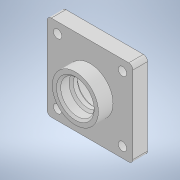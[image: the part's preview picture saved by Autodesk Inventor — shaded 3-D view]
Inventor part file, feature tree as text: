
AUTODESK INVENTOR PART (.ipt)
format: ipt  version: 2022 (Build 260153000, 153)  size: 163,840 bytes
history: native  units: mm
features: sketch x4, extrude x4, chamfer x2, projected_geometry x2, hole x1, plane x1, fillet x1
ambient origin geometry x8: Origin, YZ Plane, XZ Plane, XY Plane, X Axis, Y Axis, Z Axis, Center Point
bodies: Solid1 (feature_tree)
feature tree (15):
  sketch  "Sketch1"  dims[d0=31.0mm d1=5.0mm]
  extrude  "Extrusion1"  Depth=5.0mm
  hole  "Hole1"  [1 undecoded]
  extrude  "Extrusion2"  Depth=7.0mm TaperAngle=0.0deg
  extrude  "Extrusion3"  Depth=2.0mm
  plane  "Work Plane1"
  extrude  "Extrusion4"  TaperAngle=0.0deg  [1 undecoded]
  chamfer  "Chamfer1"  Distance=1.0mm
  fillet  "Fillet1"  Radius=4.0mm
  chamfer  "Chamfer2"  Distance=2.0mm Angle=45.0deg
  sketch  "Sketch2"  dims[d2=7.0mm d3=0.0mm]
  sketch  "Sketch3"  dims[d4=4.0mm d5=6.0mm d6=4.0mm d7=2.0mm d8=90.0deg d9=10.0mm d10=0.0mm d11=22.0mm]
  projected_geometry  "Projected Loop1"
  sketch  "Sketch4"  dims[d12=16.0mm d13=7.0mm d14=0.0mm d15=16.0mm d16=0.0mm d17=0.0mm d18=1.0mm d19=4.0mm d20=0.0mm d21=1.0mm d22=2.0mm d23=45.0deg d24=2.0mm d25=1.0mm d26=2.0mm d27=45.0deg]
  projected_geometry  "Projected Loop2"
note: 2 required parameter values undecoded (feature->parameter linkage not recoverable at this tier; creation-order binding heuristic only, values carry confidence <= 0.55)
